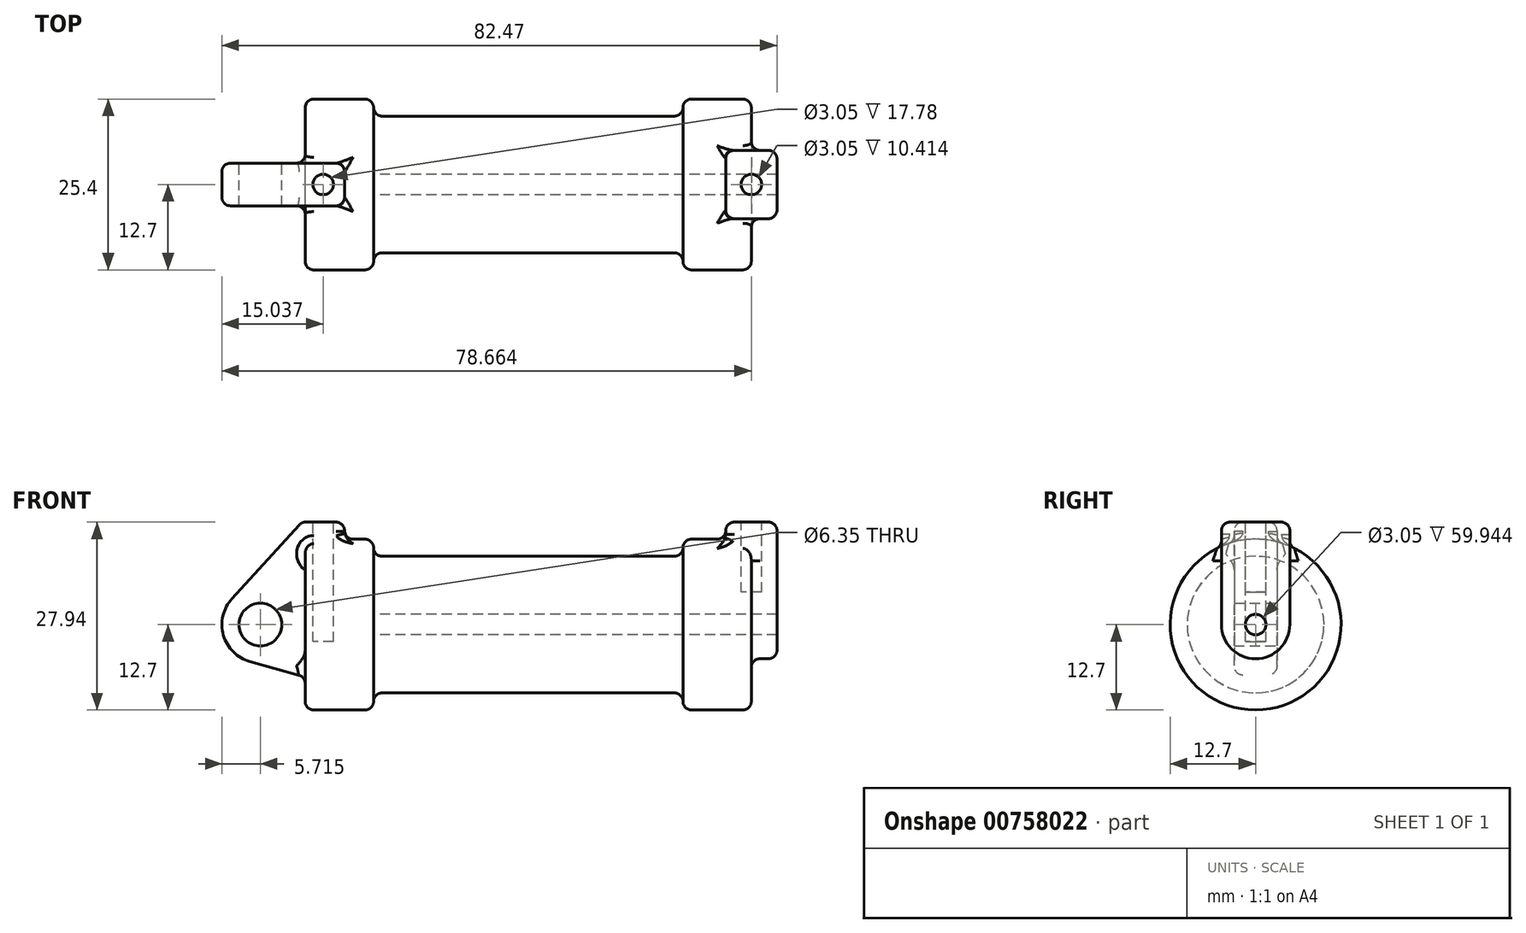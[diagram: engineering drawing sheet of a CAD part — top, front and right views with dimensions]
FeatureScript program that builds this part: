
annotation { "Feature Type Name" : "Feature", "Feature Type Description" : "" }
export const myFeature = defineFeature(function(context is Context, id is Id, definition is map)
    precondition{}
    {
        {
            var Q0;
            Q0=qCreatedBy(makeId("Front.planeOp"),FACE);
            var sketch = newSketch(context, id + "F0", { "sketchPlane" : qUnion([Q0])});
            skLineSegment(sketch, "E0", {"start": v(0, 0) * mm, "end": v(0, 12.7) * mm});
            skLineSegment(sketch, "E1", {"start": v(0, 12.7) * mm, "end": v(10.16, 12.7) * mm});
            skLineSegment(sketch, "E2", {"start": v(10.16, 12.7) * mm, "end": v(10.16, 10.16) * mm});
            skLineSegment(sketch, "E3", {"start": v(10.16, 10.16) * mm, "end": v(56.13, 10.16) * mm});
            skLineSegment(sketch, "E4", {"start": v(56.13, 10.16) * mm, "end": v(56.13, 12.7) * mm});
            skLineSegment(sketch, "E5", {"start": v(56.13, 12.7) * mm, "end": v(66.3, 12.7) * mm});
            skLineSegment(sketch, "E6", {"start": v(66.3, 12.7) * mm, "end": v(66.3, 0) * mm});
            skLineSegment(sketch, "E7", {"start": v(66.3, 0) * mm, "end": v(0, 0) * mm});
            skLineSegment(sketch, "E8", {"start": v(5.84, 15.24) * mm, "end": v(-0.5, 15.24) * mm});
            skLineSegment(sketch, "E9", {"start": v(-0.5, 15.24) * mm, "end": v(-10.88, 3.85) * mm});
            skLineSegment(sketch, "E10", {"start": v(0, 0) * mm, "end": v(-6.65, 0) * mm});
            skCircle(sketch, "E11", {"center": v(-6.65, 0) * mm, "radius": 5.72 * mm});
            skCircle(sketch, "E12", {"center": v(-6.65, 0) * mm, "radius": 3.18 * mm});
            skLineSegment(sketch, "E13", {"start": v(5.84, 15.24) * mm, "end": v(5.84, -9.4) * mm});
            skLineSegment(sketch, "E14", {"start": v(5.84, -9.4) * mm, "end": v(-8.18, -5.5) * mm});
            skSolve(sketch);
        }
        {
            var Q0;
            {var subQ0=sQuery(id+"F0.wireOp",EDGE,"E2");Q0=makeQuery(id+"F0.imprint","IMPRINT",FACE,{"disambiguationData":[TD([[makeQuery(id+"F0.imprint","IMPRINT",EDGE,{"derivedFrom":subQ0}),-1.0]])]});}
            var Q1;
            {var subQ0=sQuery(id+"F0.wireOp",EDGE,"E0");Q1=makeQuery(id+"F0.imprint","IMPRINT",FACE,{"disambiguationData":[TD([[makeQuery(id+"F0.imprint","IMPRINT",EDGE,{"derivedFrom":subQ0}),-1.0]])]});}
            var Q2;
            Q2=sQuery(id+"F0.wireOp",EDGE,"E12");
            var Q3;
            Q3=sQuery(id+"F0.wireOp",EDGE,"E7");
            revolve(context, id + "F1", {"surfaceOperationType" : NewSurfaceOperationType.NEW, "entities" : qUnion([Q0, Q1]), "surfaceEntities" : qUnion([Q2]), "axis" : qUnion([Q3]), "revolveType" : RevolveType.FULL});
        }
        {
            var Q0;
            {var subQ5=sQuery(id+"F0.wireOp",EDGE,"E12");Q0=makeQuery(id+"F0.imprint","IMPRINT",FACE,{"disambiguationData":[TD([[makeQuery(id+"F0.imprint","IMPRINT",EDGE,{"derivedFrom":subQ5}),-1.0]])]});}
            var Q1;
            {var subQ0=sQuery(id+"F0.wireOp",EDGE,"E14");Q1=makeQuery(id+"F0.imprint","IMPRINT",FACE,{"disambiguationData":[TD([[makeQuery(id+"F0.imprint","IMPRINT",EDGE,{"derivedFrom":subQ0}),-1.0]])]});}
            var Q2;
            {var subQ1=sQuery(id+"F0.wireOp",EDGE,"E0");Q2=makeQuery(id+"F0.imprint","IMPRINT",FACE,{"disambiguationData":[TD([[makeQuery(id+"F0.imprint","IMPRINT",EDGE,{"derivedFrom":subQ1}),1.0]])]});}
            var Q3;
            {var subQ0=sQuery(id+"F0.wireOp",EDGE,"E0");Q3=makeQuery(id+"F0.imprint","IMPRINT",FACE,{"disambiguationData":[TD([[makeQuery(id+"F0.imprint","IMPRINT",EDGE,{"derivedFrom":subQ0}),-1.0]])]});}
            extrude(context, id + "F2", {"entities" : qUnion([Q0, Q1, Q2, Q3]), "operationType" : NewBodyOperationType.ADD, "endBound" : BoundingType.SYMMETRIC, "depth" : 6.35 * mm, "offsetDistance" : 25.4 * mm});
        }
        {
            var Q0;
            Q0=makeQuery(id+"F1.opRevolve","SWEPT_FACE",FACE,{"disambiguationData":[OSD([sQuery(id+"F0.wireOp",EDGE,"E6")])]});
            var sketch = newSketch(context, id + "F3", { "sketchPlane" : qUnion([Q0])});
            skCircle(sketch, "E15", {"center": v(0, 0) * mm, "radius": 1.52 * mm});
            skCircle(sketch, "E16", {"center": v(0, 0) * mm, "radius": 5.08 * mm});
            skLineSegment(sketch, "E17", {"start": v(5.08, 0) * mm, "end": v(5.08, 15.24) * mm});
            skLineSegment(sketch, "E18", {"start": v(-5.08, 0) * mm, "end": v(-5.08, 15.24) * mm});
            skLineSegment(sketch, "E19", {"start": v(-5.08, 15.24) * mm, "end": v(5.08, 15.24) * mm});
            skSolve(sketch);
        }
        {
            var Q0;
            Q0 = qSketchRegion(id + "F3", true);
            extrude(context, id + "F4", {"entities" : qUnion([Q0]), "operationType" : NewBodyOperationType.ADD, "endBound" : BoundingType.SYMMETRIC, "depth" : 7.62 * mm, "offsetDistance" : 25.4 * mm});
        }
        {
            var Q0;
            Q0=makeQuery(id+"F3.imprint","IMPRINT",FACE,{"disambiguationData":[TD([[makeQuery(id+"F3.imprint","IMPRINT",EDGE,{"derivedFrom":sQuery(id+"F3.wireOp",EDGE,"E15")}),1.0]])]});
            var Q1;
            Q1=makeQuery(id+"F1.opRevolve","SWEPT_FACE",FACE,{"disambiguationData":[OSD([sQuery(id+"F0.wireOp",EDGE,"E2")])]});
            extrude(context, id + "F5", {"entities" : qUnion([Q0]), "operationType" : NewBodyOperationType.REMOVE, "endBound" : BoundingType.UP_TO_SURFACE, "oppositeDirection" : true, "depth" : 25.4 * mm, "endBoundEntityFace" : qUnion([Q1]), "offsetDistance" : 25.4 * mm});
        }
        {
            var Q0;
            Q0=makeQuery(id+"F4.opExtrude","SWEPT_FACE",FACE,{"disambiguationData":[OSD([sQuery(id+"F3.wireOp",EDGE,"E19")])]});
            var sketch = newSketch(context, id + "F6", { "sketchPlane" : qUnion([Q0])});
            skPoint(sketch, "E20.centerSnap0", {"position": v(70.1, 0) * mm});
            skPoint(sketch, "E21.centerSnap0", {"position": v(62.48, 0) * mm});
            skCircle(sketch, "E22", {"center": v(66.3, 0) * mm, "radius": 1.52 * mm});
            skPoint(sketch, "E22.centerSnap0", {"position": v(66.3, -5.08) * mm});
            skSolve(sketch);
        }
        {
            var Q0;
            Q0=makeQuery(id+"F2.opExtrude","SWEPT_FACE",FACE,{"disambiguationData":[OSD([sQuery(id+"F0.wireOp",EDGE,"E8")])]});
            var sketch = newSketch(context, id + "F7", { "sketchPlane" : qUnion([Q0])});
            skCircle(sketch, "E23", {"center": v(2.67, 0) * mm, "radius": 1.52 * mm});
            skPoint(sketch, "E23.centerSnap0", {"position": v(5.84, 0) * mm});
            skPoint(sketch, "E23.centerSnap1", {"position": v(2.67, -3.18) * mm});
            skSolve(sketch);
        }
        {
            var Q0;
            Q0 = qSketchRegion(id + "F7", true);
            extrude(context, id + "F8", {"entities" : qUnion([Q0]), "operationType" : NewBodyOperationType.REMOVE, "oppositeDirection" : true, "depth" : 17.78 * mm, "offsetDistance" : 25.4 * mm});
        }
        {
            var Q0;
            Q0 = qSketchRegion(id + "F6", true);
            extrude(context, id + "F9", {"entities" : qUnion([Q0]), "operationType" : NewBodyOperationType.REMOVE, "oppositeDirection" : true, "depth" : 10.4 * mm, "offsetDistance" : 25.4 * mm});
        }
        {
            var Q0;
            Q0=makeQuery(id+"F1.opRevolve","SWEPT_EDGE",EDGE,{"disambiguationData":[OSD([sQuery(id+"F0.wireOp",EDGE,"E2"),sQuery(id+"F0.wireOp",EDGE,"E3")])]});
            var Q1;
            Q1=makeQuery(id+"F1.opRevolve","SWEPT_EDGE",EDGE,{"disambiguationData":[OSD([sQuery(id+"F0.wireOp",EDGE,"E1"),sQuery(id+"F0.wireOp",EDGE,"E2")])]});
            var Q2;
            Q2=makeQuery(id+"F1.opRevolve","SWEPT_EDGE",EDGE,{"disambiguationData":[OSD([sQuery(id+"F0.wireOp",EDGE,"E3"),sQuery(id+"F0.wireOp",EDGE,"E4")])]});
            var Q3;
            Q3=makeQuery(id+"F1.opRevolve","SWEPT_EDGE",EDGE,{"disambiguationData":[OSD([sQuery(id+"F0.wireOp",EDGE,"E4"),sQuery(id+"F0.wireOp",EDGE,"E5")])]});
            var Q4;
            Q4=makeQuery(id+"F1.opRevolve","SWEPT_FACE",FACE,{"disambiguationData":[OSD([sQuery(id+"F0.wireOp",EDGE,"E1")])]});
            var Q5;
            Q5=makeQuery(id+"F1.opRevolve","SWEPT_FACE",FACE,{"disambiguationData":[OSD([sQuery(id+"F0.wireOp",EDGE,"E3")])]});
            var Q6;
            Q6=makeQuery(id+"F1.opRevolve","SWEPT_FACE",FACE,{"disambiguationData":[OSD([sQuery(id+"F0.wireOp",EDGE,"E5")])]});
            fillet(context, id + "F10", {"entities" : qUnion([Q0, Q1, Q2, Q3, Q4, Q5, Q6]), "radius" : 1.27 * mm, "tangentPropagation" : true, "allowEdgeOverflow" : false});
        }
        {
            var Q0;
            Q0=makeQuery(id+"F4.opExtrude","SWEPT_FACE",FACE,{"disambiguationData":[OSD([sQuery(id+"F3.wireOp",EDGE,"E18")])]});
            var Q1;
            Q1=makeQuery(id+"F4.opExtrude","CAP_EDGE",EDGE,{"disambiguationData":[OSD([sQuery(id+"F3.wireOp",EDGE,"E19")])],"isStart":false});
            var Q2;
            Q2=makeQuery(id+"F4.opExtrude","CAP_EDGE",EDGE,{"disambiguationData":[OSD([sQuery(id+"F3.wireOp",EDGE,"E19")])],"isStart":true});
            var Q3;
            Q3=makeQuery(id+"F4.opExtrude","SWEPT_EDGE",EDGE,{"disambiguationData":[OSD([sQuery(id+"F3.wireOp",EDGE,"E17"),sQuery(id+"F3.wireOp",EDGE,"E19")])]});
            var Q4;
            Q4=makeQuery(id+"F4.opExtrude","CAP_EDGE",EDGE,{"disambiguationData":[OSD([sQuery(id+"F3.wireOp",EDGE,"E17")])],"isStart":false});
            var Q5;
            Q5=makeQuery(id+"F4.opExtrude","CAP_EDGE",EDGE,{"disambiguationData":[OSD([sQuery(id+"F3.wireOp",EDGE,"E16")])],"isStart":false});
            var Q6;
            {var subQ0=makeQuery(id+"F4.opExtrude","SWEPT_FACE",FACE,{"disambiguationData":[OSD([sQuery(id+"F3.wireOp",EDGE,"E16")])]});Q6=makeQuery(id+"F10.opFillet","BLEND_EDGE",EDGE,{"blendedFrom":[makeQuery(id+"F4.boolean.opBoolean","INTERSECT",EDGE,{"derivedFrom":[makeQuery(id+"F1.opRevolve","SWEPT_FACE",FACE,{"disambiguationData":[OSD([sQuery(id+"F0.wireOp",EDGE,"E6")])]}),subQ0]}),subQ0],"blendedInto":[subQ0]});}
            var Q7;
            Q7=makeQuery(id+"F4.opExtrude","CAP_EDGE",EDGE,{"disambiguationData":[OSD([sQuery(id+"F3.wireOp",EDGE,"E17")])],"isStart":true});
            var Q8;
            {var subQ0=sQuery(id+"F3.wireOp",EDGE,"E17");Q8=makeQuery(id+"F10.opFillet","BLEND_EDGE",EDGE,{"blendedFrom":[makeQuery(id+"F4.boolean.opBoolean","INTERSECT",EDGE,{"derivedFrom":[makeQuery(id+"F1.opRevolve","SWEPT_FACE",FACE,{"disambiguationData":[OSD([sQuery(id+"F0.wireOp",EDGE,"E5")])]}),makeQuery(id+"F4.opExtrude","CAP_FACE",FACE,{"disambiguationData":[OSD([sQuery(id+"F3.wireOp",EDGE,"E15"),sQuery(id+"F3.wireOp",EDGE,"E16"),subQ0,sQuery(id+"F3.wireOp",EDGE,"E18"),sQuery(id+"F3.wireOp",EDGE,"E19")])],"isStart":true})]}),makeQuery(id+"F4.opExtrude","SWEPT_FACE",FACE,{"disambiguationData":[OSD([subQ0])]})],"blendedInto":[makeQuery(id+"F4.opExtrude","SWEPT_FACE",FACE,{"disambiguationData":[OSD([subQ0])]})]});}
            var Q9;
            Q9=makeQuery(id+"F4.opExtrude","SWEPT_FACE",FACE,{"disambiguationData":[OSD([sQuery(id+"F3.wireOp",EDGE,"E17")])]});
            fillet(context, id + "F11", {"entities" : qUnion([Q0, Q1, Q2, Q3, Q4, Q5, Q6, Q7, Q8, Q9]), "radius" : 1.27 * mm, "tangentPropagation" : true, "allowEdgeOverflow" : false});
        }
        {
            var Q0;
            Q0=makeQuery(id+"F2.opExtrude","SWEPT_FACE",FACE,{"disambiguationData":[OSD([sQuery(id+"F0.wireOp",EDGE,"E9")])]});
            var Q1;
            Q1=makeQuery(id+"F2.opExtrude","SWEPT_FACE",FACE,{"disambiguationData":[OSD([sQuery(id+"F0.wireOp",EDGE,"E11")])]});
            var Q2;
            {var subQ0=sQuery(id+"F0.wireOp",EDGE,"E14");var subQ1=sQuery(id+"F0.wireOp",EDGE,"E13");var subQ2=sQuery(id+"F0.wireOp",EDGE,"E12");var subQ3=sQuery(id+"F0.wireOp",EDGE,"E11");var subQ4=sQuery(id+"F0.wireOp",EDGE,"E9");var subQ5=sQuery(id+"F0.wireOp",EDGE,"E8");var subQ6=sQuery(id+"F0.wireOp",EDGE,"E0");Q2=makeQuery(id+"F10.opFillet","BLEND_FACE",FACE,{"disambiguationData":[OSD([subQ6,subQ5,subQ4,subQ3,subQ2,subQ1,subQ0]),TDD([makeQuery(id+"F2.boolean.opBoolean","INTERSECT",EDGE,{"derivedFrom":[makeQuery(id+"F1.opRevolve","SWEPT_FACE",FACE,{"disambiguationData":[OSD([subQ6])]}),makeQuery(id+"F2.opExtrude","CAP_FACE",FACE,{"disambiguationData":[OSD([subQ5,subQ4,subQ3,subQ2,subQ1,subQ0])],"isStart":true})]})])]});}
            var Q3;
            {var subQ0=makeQuery(id+"F1.opRevolve","SWEPT_FACE",FACE,{"disambiguationData":[OSD([sQuery(id+"F0.wireOp",EDGE,"E0")])]});Q3=makeQuery(id+"F10.opFillet","BLEND_EDGE",EDGE,{"blendedFrom":[makeQuery(id+"F2.boolean.opBoolean","INTERSECT",EDGE,{"derivedFrom":[subQ0,makeQuery(id+"F2.opExtrude","CAP_FACE",FACE,{"disambiguationData":[OSD([sQuery(id+"F0.wireOp",EDGE,"E8"),sQuery(id+"F0.wireOp",EDGE,"E9"),sQuery(id+"F0.wireOp",EDGE,"E11"),sQuery(id+"F0.wireOp",EDGE,"E12"),sQuery(id+"F0.wireOp",EDGE,"E13"),sQuery(id+"F0.wireOp",EDGE,"E14")])],"isStart":false})]}),subQ0],"blendedInto":[subQ0]});}
            var Q4;
            {var subQ0=sQuery(id+"F0.wireOp",EDGE,"E14");var subQ1=sQuery(id+"F0.wireOp",EDGE,"E13");var subQ2=sQuery(id+"F0.wireOp",EDGE,"E12");var subQ3=sQuery(id+"F0.wireOp",EDGE,"E11");var subQ4=sQuery(id+"F0.wireOp",EDGE,"E9");var subQ5=sQuery(id+"F0.wireOp",EDGE,"E8");var subQ6=sQuery(id+"F0.wireOp",EDGE,"E0");Q4=makeQuery(id+"F10.opFillet","BLEND_FACE",FACE,{"disambiguationData":[OSD([subQ6,subQ5,subQ4,subQ3,subQ2,subQ1,subQ0]),TDD([makeQuery(id+"F2.boolean.opBoolean","INTERSECT",EDGE,{"derivedFrom":[makeQuery(id+"F1.opRevolve","SWEPT_FACE",FACE,{"disambiguationData":[OSD([subQ6])]}),makeQuery(id+"F2.opExtrude","CAP_FACE",FACE,{"disambiguationData":[OSD([subQ5,subQ4,subQ3,subQ2,subQ1,subQ0])],"isStart":false})]})])]});}
            var Q5;
            {var subQ0=sQuery(id+"F0.wireOp",EDGE,"E14");var subQ1=sQuery(id+"F0.wireOp",EDGE,"E13");var subQ2=sQuery(id+"F0.wireOp",EDGE,"E12");var subQ3=sQuery(id+"F0.wireOp",EDGE,"E11");var subQ4=sQuery(id+"F0.wireOp",EDGE,"E9");var subQ5=sQuery(id+"F0.wireOp",EDGE,"E8");var subQ6=sQuery(id+"F0.wireOp",EDGE,"E1");var subQ7=sQuery(id+"F0.wireOp",EDGE,"E0");Q5=makeQuery(id+"F10.opFillet","BLEND_FACE",FACE,{"disambiguationData":[OSD([subQ7,subQ6,subQ5,subQ4,subQ3,subQ2,subQ1,subQ0]),TDD([makeQuery(id+"F2.boolean.opBoolean","INTERSECT",VERTEX,{"derivedFrom":[makeQuery(id+"F1.opRevolve","SWEPT_FACE",FACE,{"disambiguationData":[OSD([subQ7])]}),makeQuery(id+"F1.opRevolve","SWEPT_FACE",FACE,{"disambiguationData":[OSD([subQ6])]}),makeQuery(id+"F2.opExtrude","CAP_FACE",FACE,{"disambiguationData":[OSD([subQ5,subQ4,subQ3,subQ2,subQ1,subQ0])],"isStart":false})]})])]});}
            var Q6;
            {var subQ0=sQuery(id+"F0.wireOp",EDGE,"E14");var subQ1=sQuery(id+"F0.wireOp",EDGE,"E13");var subQ2=sQuery(id+"F0.wireOp",EDGE,"E12");var subQ3=sQuery(id+"F0.wireOp",EDGE,"E11");var subQ4=sQuery(id+"F0.wireOp",EDGE,"E9");var subQ5=sQuery(id+"F0.wireOp",EDGE,"E8");var subQ6=sQuery(id+"F0.wireOp",EDGE,"E1");var subQ7=sQuery(id+"F0.wireOp",EDGE,"E0");Q6=makeQuery(id+"F10.opFillet","BLEND_FACE",FACE,{"disambiguationData":[OSD([subQ7,subQ6,subQ5,subQ4,subQ3,subQ2,subQ1,subQ0]),TDD([makeQuery(id+"F2.boolean.opBoolean","INTERSECT",VERTEX,{"derivedFrom":[makeQuery(id+"F1.opRevolve","SWEPT_FACE",FACE,{"disambiguationData":[OSD([subQ7])]}),makeQuery(id+"F1.opRevolve","SWEPT_FACE",FACE,{"disambiguationData":[OSD([subQ6])]}),makeQuery(id+"F2.opExtrude","CAP_FACE",FACE,{"disambiguationData":[OSD([subQ5,subQ4,subQ3,subQ2,subQ1,subQ0])],"isStart":true})]})])]});}
            var Q7;
            Q7=makeQuery(id+"F2.opExtrude","SWEPT_EDGE",EDGE,{"disambiguationData":[OSD([sQuery(id+"F0.wireOp",EDGE,"E8"),sQuery(id+"F0.wireOp",EDGE,"E13")])]});
            var Q8;
            Q8=makeQuery(id+"F2.opExtrude","CAP_EDGE",EDGE,{"disambiguationData":[OSD([sQuery(id+"F0.wireOp",EDGE,"E8")])],"isStart":true});
            var Q9;
            Q9=makeQuery(id+"F2.opExtrude","SWEPT_FACE",FACE,{"disambiguationData":[OSD([sQuery(id+"F0.wireOp",EDGE,"E14")])]});
            var Q10;
            Q10=makeQuery(id+"F2.opExtrude","CAP_EDGE",EDGE,{"disambiguationData":[OSD([sQuery(id+"F0.wireOp",EDGE,"E8")])],"isStart":false});
            var Q11;
            Q11=makeQuery(id+"F2.opExtrude","SWEPT_FACE",FACE,{"disambiguationData":[OSD([sQuery(id+"F0.wireOp",EDGE,"E13")])]});
            fillet(context, id + "F12", {"entities" : qUnion([Q0, Q1, Q2, Q3, Q4, Q5, Q6, Q7, Q8, Q9, Q10, Q11]), "radius" : 1.27 * mm, "tangentPropagation" : true, "allowEdgeOverflow" : false});
        }
    });
